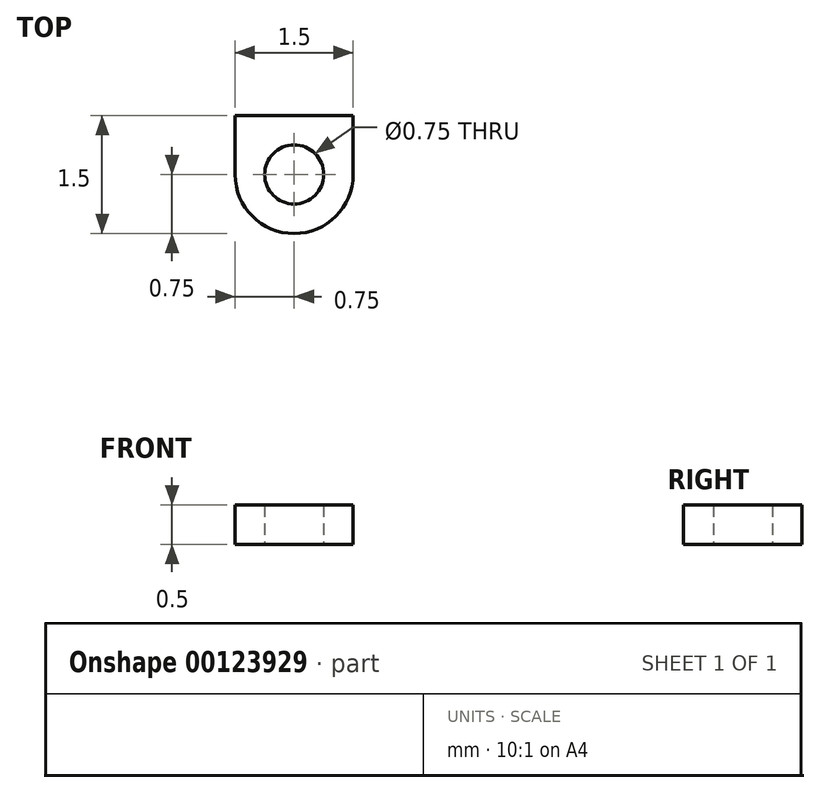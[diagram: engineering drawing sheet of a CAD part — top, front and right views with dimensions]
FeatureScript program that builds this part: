
annotation { "Feature Type Name" : "Feature", "Feature Type Description" : "" }
export const myFeature = defineFeature(function(context is Context, id is Id, definition is map)
    precondition{}
    {
        {
            var Q0;
            Q0=qCreatedBy(makeId("Top.planeOp"),FACE);
            var sketch = newSketch(context, id + "F0", { "sketchPlane" : qUnion([Q0])});
            skArc(sketch, "E0", {"start": v(-0.75, 0) * mm, "mid": v(0, -0.75) * mm, "end": v(0.75, 0) * mm});
            skLineSegment(sketch, "E1", {"start": v(-0.75, 0) * mm, "end": v(-0.75, 0.75) * mm});
            skLineSegment(sketch, "E2", {"start": v(0.75, 0) * mm, "end": v(0.75, 0.75) * mm});
            skCircle(sketch, "E3", {"center": v(0, 0) * mm, "radius": 0.38 * mm});
            skLineSegment(sketch, "E4", {"start": v(-0.75, 0.75) * mm, "end": v(0.75, 0.75) * mm});
            skSolve(sketch);
        }
        {
            var Q0;
            Q0 = qSketchRegion(id + "F0", true);
            extrude(context, id + "F1", {"entities" : qUnion([Q0]), "depth" : 0.5 * mm});
        }
    });
